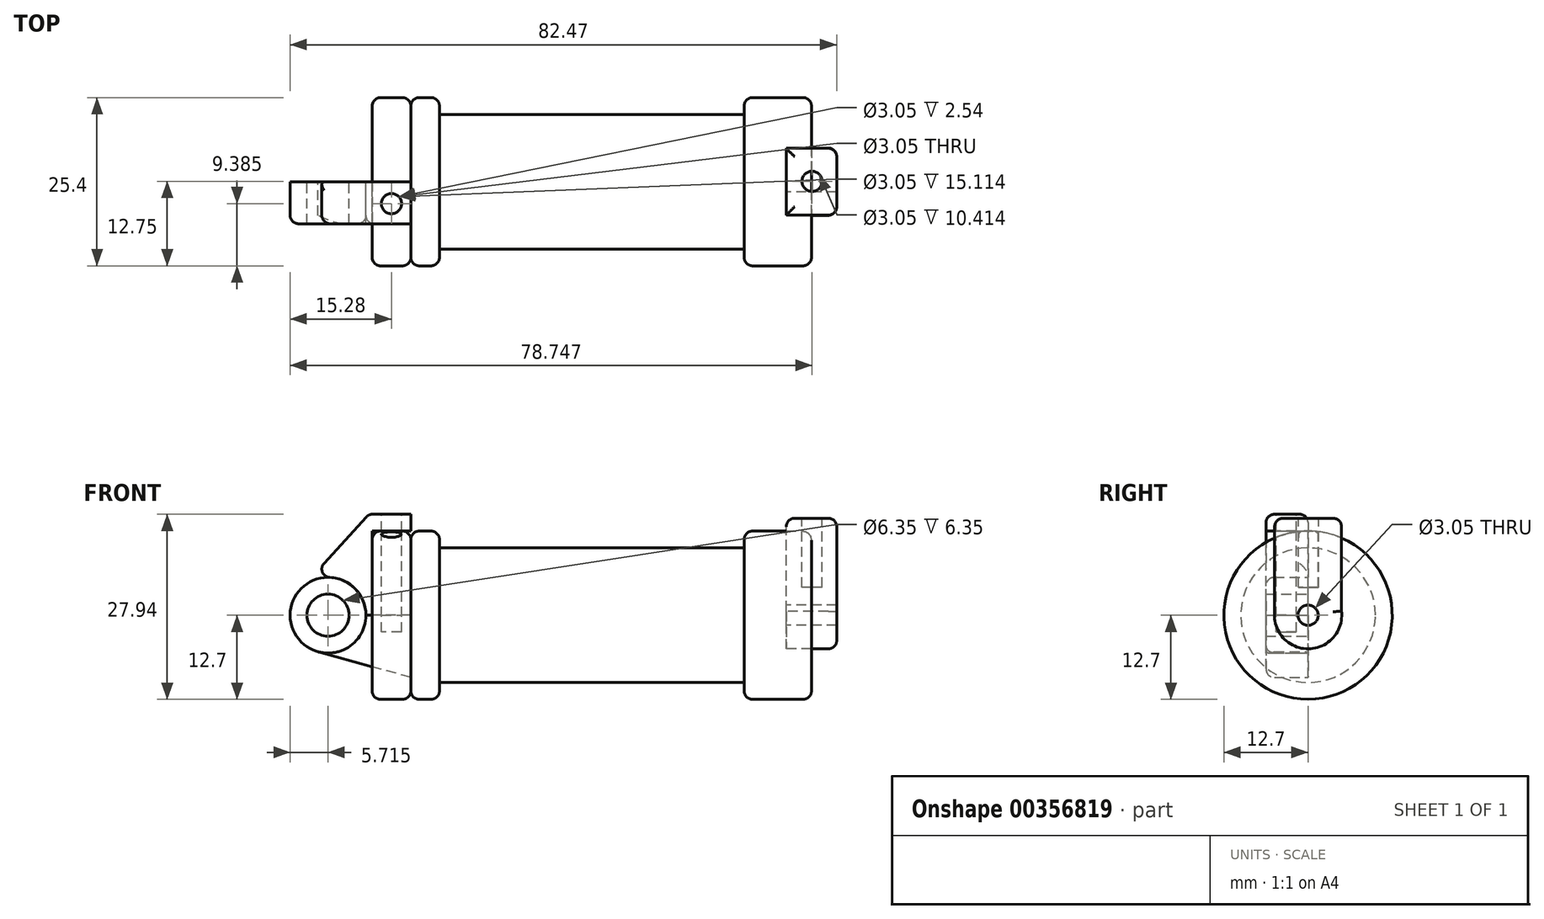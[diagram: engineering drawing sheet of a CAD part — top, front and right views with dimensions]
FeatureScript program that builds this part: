
annotation { "Feature Type Name" : "Feature", "Feature Type Description" : "" }
export const myFeature = defineFeature(function(context is Context, id is Id, definition is map)
    precondition{}
    {
        {
            var Q0;
            Q0=qCreatedBy(makeId("Front.planeOp"),FACE);
            var sketch = newSketch(context, id + "F0", { "sketchPlane" : qUnion([Q0])});
            skLineSegment(sketch, "E0", {"start": v(0, 0) * mm, "end": v(0, 12.7) * mm});
            skLineSegment(sketch, "E1", {"start": v(0, 12.7) * mm, "end": v(10.16, 12.7) * mm});
            skLineSegment(sketch, "E2", {"start": v(10.16, 12.7) * mm, "end": v(10.16, 10.16) * mm});
            skLineSegment(sketch, "E3", {"start": v(10.16, 10.16) * mm, "end": v(56.13, 10.16) * mm});
            skLineSegment(sketch, "E4", {"start": v(56.13, 10.16) * mm, "end": v(56.13, 12.7) * mm});
            skLineSegment(sketch, "E5", {"start": v(56.13, 12.7) * mm, "end": v(66.3, 12.7) * mm});
            skLineSegment(sketch, "E6", {"start": v(66.3, 12.7) * mm, "end": v(66.3, 0) * mm});
            skLineSegment(sketch, "E7", {"start": v(66.3, 0) * mm, "end": v(0, 0) * mm});
            skLineSegment(sketch, "E8", {"start": v(5.84, 15.24) * mm, "end": v(-0.5, 15.24) * mm});
            skLineSegment(sketch, "E9", {"start": v(-0.5, 15.24) * mm, "end": v(-10.88, 3.85) * mm});
            skLineSegment(sketch, "E10", {"start": v(0, 0) * mm, "end": v(-6.65, 0) * mm});
            skCircle(sketch, "E11", {"center": v(-6.65, 0) * mm, "radius": 5.72 * mm});
            skCircle(sketch, "E12", {"center": v(-6.65, 0) * mm, "radius": 3.18 * mm});
            skLineSegment(sketch, "E13", {"start": v(5.84, 15.24) * mm, "end": v(5.84, -9.4) * mm});
            skLineSegment(sketch, "E14", {"start": v(5.84, -9.4) * mm, "end": v(-8.18, -5.5) * mm});
            skSolve(sketch);
        }
        {
            var Q0;
            {var subQ0=sQuery(id+"F0.wireOp",EDGE,"E2");Q0=makeQuery(id+"F0.imprint","IMPRINT",FACE,{"disambiguationData":[TD([[makeQuery(id+"F0.imprint","IMPRINT",EDGE,{"derivedFrom":subQ0}),-1.0]])]});}
            var Q1;
            Q1=sQuery(id+"F0.wireOp",EDGE,"E7");
            revolve(context, id + "F1", {"entities" : qUnion([Q0]), "axis" : qUnion([Q1]), "revolveType" : RevolveType.FULL});
        }
        {
            var Q0;
            {var subQ1=sQuery(id+"F0.wireOp",EDGE,"E0");Q0=makeQuery(id+"F0.imprint","IMPRINT",FACE,{"disambiguationData":[TD([[makeQuery(id+"F0.imprint","IMPRINT",EDGE,{"derivedFrom":subQ1}),1.0]])]});}
            extrude(context, id + "F2", {"entities" : qUnion([Q0]), "depth" : 6.35 * mm});
        }
        {
            var Q0;
            {var subQ0=sQuery(id+"F0.wireOp",EDGE,"E0");Q0=makeQuery(id+"F0.imprint","IMPRINT",FACE,{"disambiguationData":[TD([[makeQuery(id+"F0.imprint","IMPRINT",EDGE,{"derivedFrom":subQ0}),-1.0]])]});}
            var Q1;
            Q1=sQuery(id+"F0.wireOp",EDGE,"E7");
            revolve(context, id + "F3", {"entities" : qUnion([Q0]), "axis" : qUnion([Q1]), "revolveType" : RevolveType.FULL});
        }
        {
            var Q0;
            {var subQ0=sQuery(id+"F0.wireOp",EDGE,"E14");Q0=makeQuery(id+"F0.imprint","IMPRINT",FACE,{"disambiguationData":[TD([[makeQuery(id+"F0.imprint","IMPRINT",EDGE,{"derivedFrom":subQ0}),-1.0]])]});}
            extrude(context, id + "F4", {"entities" : qUnion([Q0]), "depth" : 6.35 * mm});
        }
        {
            var Q0;
            {var subQ5=sQuery(id+"F0.wireOp",EDGE,"E12");Q0=makeQuery(id+"F0.imprint","IMPRINT",FACE,{"disambiguationData":[TD([[makeQuery(id+"F0.imprint","IMPRINT",EDGE,{"derivedFrom":subQ5}),-1.0]])]});}
            extrude(context, id + "F5", {"entities" : qUnion([Q0]), "depth" : 6.35 * mm});
        }
        {
            var Q0;
            Q0=makeQuery(id+"F1.opRevolve","SWEPT_FACE",FACE,{"disambiguationData":[OSD([sQuery(id+"F0.wireOp",EDGE,"E6")])]});
            var sketch = newSketch(context, id + "F6", { "sketchPlane" : qUnion([Q0])});
            skCircle(sketch, "E15", {"center": v(0, 0) * mm, "radius": 1.52 * mm});
            skCircle(sketch, "E16", {"center": v(0, 0) * mm, "radius": 5.08 * mm});
            skLineSegment(sketch, "E17", {"start": v(5.04, -0.6) * mm, "end": v(5.04, 14.64) * mm});
            skLineSegment(sketch, "E18", {"start": v(-5.04, -0.6) * mm, "end": v(-5.04, 14.64) * mm});
            skLineSegment(sketch, "E19", {"start": v(-5.04, 14.64) * mm, "end": v(5.04, 14.64) * mm});
            skSolve(sketch);
        }
        {
            var Q0;
            Q0 = qSketchRegion(id + "F6", true);
            extrude(context, id + "F7", {"entities" : qUnion([Q0]), "endBound" : BoundingType.SYMMETRIC, "depth" : 7.62 * mm});
        }
        {
            var Q0;
            Q0=makeQuery(id+"F7.opExtrude","SWEPT_FACE",FACE,{"disambiguationData":[OSD([sQuery(id+"F6.wireOp",EDGE,"E19")])]});
            var sketch = newSketch(context, id + "F8", { "sketchPlane" : qUnion([Q0])});
            skCircle(sketch, "E20", {"center": v(66.38, 0.05) * mm, "radius": 1.52 * mm});
            skSolve(sketch);
        }
        {
            var Q0;
            Q0=makeQuery(id+"F2.opExtrude","SWEPT_FACE",FACE,{"disambiguationData":[OSD([sQuery(id+"F0.wireOp",EDGE,"E8")])]});
            var sketch = newSketch(context, id + "F9", { "sketchPlane" : qUnion([Q0])});
            skCircle(sketch, "E21", {"center": v(2.91, -3.32) * mm, "radius": 1.52 * mm});
            skSolve(sketch);
        }
        {
            var Q0;
            Q0 = qSketchRegion(id + "F9", true);
            extrude(context, id + "F10", {"entities" : qUnion([Q0]), "operationType" : NewBodyOperationType.REMOVE, "oppositeDirection" : true, "depth" : 17.78 * mm});
        }
        {
            var Q0;
            Q0 = qSketchRegion(id + "F8", true);
            extrude(context, id + "F11", {"entities" : qUnion([Q0]), "operationType" : NewBodyOperationType.REMOVE, "oppositeDirection" : true, "depth" : 10.4 * mm});
        }
        {
            var Q0;
            Q0=makeQuery(id+"F7.opExtrude","CAP_EDGE",EDGE,{"disambiguationData":[OSD([sQuery(id+"F6.wireOp",EDGE,"E18")])],"isStart":false});
            var Q1;
            Q1=makeQuery(id+"F7.opExtrude","CAP_EDGE",EDGE,{"disambiguationData":[OSD([sQuery(id+"F6.wireOp",EDGE,"E17")])],"isStart":false});
            var Q2;
            Q2=makeQuery(id+"F7.opExtrude","CAP_EDGE",EDGE,{"disambiguationData":[OSD([sQuery(id+"F6.wireOp",EDGE,"E16")])],"isStart":false});
            var Q3;
            Q3=makeQuery(id+"F7.opExtrude","CAP_EDGE",EDGE,{"disambiguationData":[OSD([sQuery(id+"F6.wireOp",EDGE,"E19")])],"isStart":false});
            var Q4;
            Q4=makeQuery(id+"F7.opExtrude","SWEPT_EDGE",EDGE,{"disambiguationData":[OSD([sQuery(id+"F6.wireOp",EDGE,"E17"),sQuery(id+"F6.wireOp",EDGE,"E19")])]});
            var Q5;
            Q5=makeQuery(id+"F7.opExtrude","SWEPT_EDGE",EDGE,{"disambiguationData":[OSD([sQuery(id+"F6.wireOp",EDGE,"E18"),sQuery(id+"F6.wireOp",EDGE,"E19")])]});
            var Q6;
            Q6=makeQuery(id+"F7.opExtrude","CAP_EDGE",EDGE,{"disambiguationData":[OSD([sQuery(id+"F6.wireOp",EDGE,"E19")])],"isStart":true});
            var Q7;
            Q7=makeQuery(id+"F7.opExtrude","SWEPT_EDGE",EDGE,{"disambiguationData":[OSD([sQuery(id+"F6.wireOp",EDGE,"E16"),sQuery(id+"F6.wireOp",EDGE,"E18")])]});
            var Q8;
            Q8=makeQuery(id+"F1.opRevolve","SWEPT_EDGE",EDGE,{"disambiguationData":[OSD([sQuery(id+"F0.wireOp",EDGE,"E1"),sQuery(id+"F0.wireOp",EDGE,"E13")])]});
            fillet(context, id + "F12", {"entities" : qUnion([Q0, Q1, Q2, Q3, Q4, Q5, Q6, Q7, Q8]), "radius" : 1.27 * mm, "tangentPropagation" : true, "allowEdgeOverflow" : false});
        }
        {
            var Q0;
            Q0=makeQuery(id+"F1.opRevolve","SWEPT_EDGE",EDGE,{"disambiguationData":[OSD([sQuery(id+"F0.wireOp",EDGE,"E5"),sQuery(id+"F0.wireOp",EDGE,"E6")])]});
            var Q1;
            Q1=makeQuery(id+"F1.opRevolve","SWEPT_EDGE",EDGE,{"disambiguationData":[OSD([sQuery(id+"F0.wireOp",EDGE,"E4"),sQuery(id+"F0.wireOp",EDGE,"E5")])]});
            fillet(context, id + "F13", {"entities" : qUnion([Q0, Q1]), "radius" : 1.27 * mm, "tangentPropagation" : true, "allowEdgeOverflow" : false});
        }
        {
            var Q0;
            Q0=makeQuery(id+"F1.opRevolve","SWEPT_EDGE",EDGE,{"disambiguationData":[OSD([sQuery(id+"F0.wireOp",EDGE,"E1"),sQuery(id+"F0.wireOp",EDGE,"E2")])]});
            var Q1;
            {var subQ0=sQuery(id+"F0.wireOp",EDGE,"E1");Q1=makeQuery(id+"F12.opFillet","BLEND_EDGE",EDGE,{"blendedFrom":[makeQuery(id+"F1.opRevolve","SWEPT_EDGE",EDGE,{"disambiguationData":[OSD([subQ0,sQuery(id+"F0.wireOp",EDGE,"E13")])]}),makeQuery(id+"F1.opRevolve","SWEPT_FACE",FACE,{"disambiguationData":[OSD([subQ0])]})],"blendedInto":[makeQuery(id+"F1.opRevolve","SWEPT_FACE",FACE,{"disambiguationData":[OSD([subQ0])]})]});}
            var Q2;
            Q2=makeQuery(id+"F3.opRevolve","SWEPT_EDGE",EDGE,{"disambiguationData":[OSD([sQuery(id+"F0.wireOp",EDGE,"E1"),sQuery(id+"F0.wireOp",EDGE,"E13")])]});
            var Q3;
            Q3=makeQuery(id+"F3.opRevolve","SWEPT_EDGE",EDGE,{"disambiguationData":[OSD([sQuery(id+"F0.wireOp",EDGE,"E0"),sQuery(id+"F0.wireOp",EDGE,"E1")])]});
            var Q4;
            Q4=makeQuery(id+"F2.opExtrude","CAP_EDGE",EDGE,{"disambiguationData":[OSD([sQuery(id+"F0.wireOp",EDGE,"E8")])],"isStart":false});
            var Q5;
            Q5=makeQuery(id+"F2.opExtrude","CAP_EDGE",EDGE,{"disambiguationData":[OSD([sQuery(id+"F0.wireOp",EDGE,"E9")])],"isStart":true});
            var Q6;
            Q6=makeQuery(id+"F2.opExtrude","CAP_EDGE",EDGE,{"disambiguationData":[OSD([sQuery(id+"F0.wireOp",EDGE,"E9")])],"isStart":false});
            var Q7;
            Q7=makeQuery(id+"F2.opExtrude","SWEPT_EDGE",EDGE,{"disambiguationData":[OSD([sQuery(id+"F0.wireOp",EDGE,"E9"),sQuery(id+"F0.wireOp",EDGE,"E11")])]});
            var Q8;
            Q8=makeQuery(id+"F2.opExtrude","SWEPT_EDGE",EDGE,{"disambiguationData":[OSD([sQuery(id+"F0.wireOp",EDGE,"E8"),sQuery(id+"F0.wireOp",EDGE,"E9")])]});
            var Q9;
            Q9=makeQuery(id+"F2.opExtrude","CAP_EDGE",EDGE,{"disambiguationData":[OSD([sQuery(id+"F0.wireOp",EDGE,"E8")])],"isStart":true});
            var Q10;
            Q10=makeQuery(id+"F2.opExtrude","CAP_EDGE",EDGE,{"disambiguationData":[OSD([sQuery(id+"F0.wireOp",EDGE,"E11")])],"isStart":false});
            var Q11;
            Q11=makeQuery(id+"F5.opExtrude","CAP_EDGE",EDGE,{"disambiguationData":[OSD([sQuery(id+"F0.wireOp",EDGE,"E11")])],"isStart":false});
            var Q12;
            Q12=makeQuery(id+"F4.opExtrude","CAP_EDGE",EDGE,{"disambiguationData":[OSD([sQuery(id+"F0.wireOp",EDGE,"E14")])],"isStart":false});
            fillet(context, id + "F14", {"entities" : qUnion([Q0, Q1, Q2, Q3, Q4, Q5, Q6, Q7, Q8, Q9, Q10, Q11, Q12]), "radius" : 1.27 * mm, "tangentPropagation" : true, "allowEdgeOverflow" : false});
        }
    });
